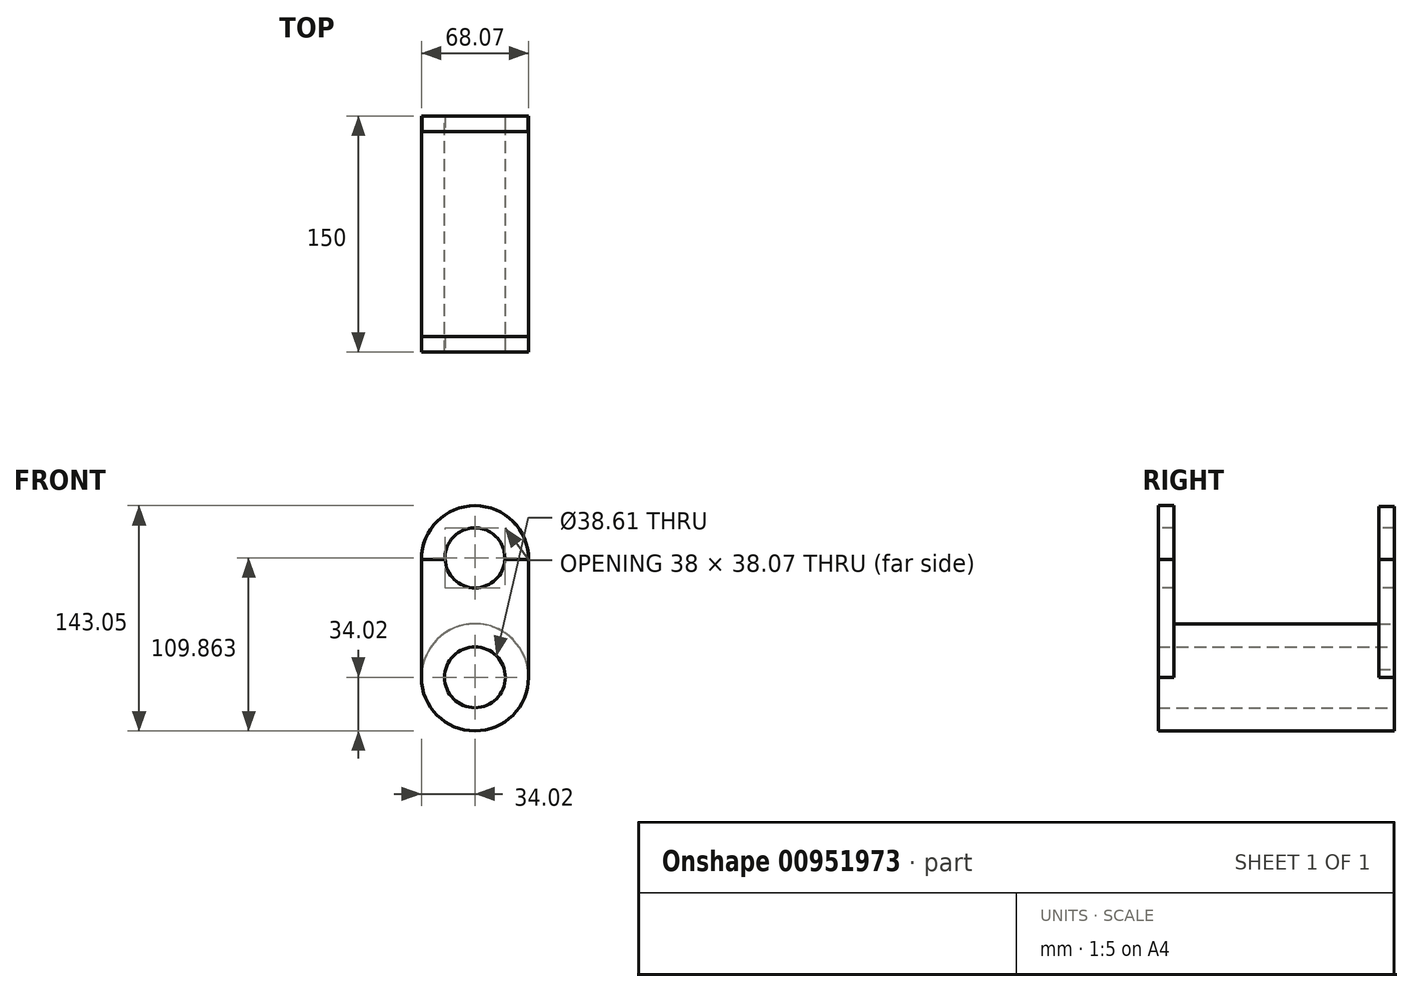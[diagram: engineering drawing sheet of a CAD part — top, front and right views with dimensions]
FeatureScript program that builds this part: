
annotation { "Feature Type Name" : "Feature", "Feature Type Description" : "" }
export const myFeature = defineFeature(function(context is Context, id is Id, definition is map)
    precondition{}
    {
        {
            var Q0;
            Q0=qCreatedBy(makeId("Front.planeOp"),FACE);
            var sketch = newSketch(context, id + "F0", { "sketchPlane" : qUnion([Q0])});
            skCircle(sketch, "E0", {"center": v(0, 0) * mm, "radius": 34.02 * mm});
            skCircle(sketch, "E1", {"center": v(0, 0) * mm, "radius": 19.3 * mm});
            skSolve(sketch);
        }
        {
            var Q0;
            Q0=makeQuery(id+"F0.imprint","IMPRINT",FACE,{"disambiguationData":[TD([[makeQuery(id+"F0.imprint","IMPRINT",EDGE,{"derivedFrom":sQuery(id+"F0.wireOp",EDGE,"E0")}),1.0]])]});
            extrude(context, id + "F1", {"entities" : qUnion([Q0]), "depth" : 75 * mm, "offsetDistance" : 25 * mm});
        }
        {
            var Q0;
            Q0=makeQuery(id+"F1.opExtrude","SWEPT_BODY",BODY,{"disambiguationData":[OSD([sQuery(id+"F0.wireOp",EDGE,"E0"),sQuery(id+"F0.wireOp",EDGE,"E1")])]});
            var Q1;
            Q1=makeQuery(id+"F1.opExtrude","CAP_FACE",FACE,{"disambiguationData":[OSD([sQuery(id+"F0.wireOp",EDGE,"E0"),sQuery(id+"F0.wireOp",EDGE,"E1")])],"isStart":true});
            mirror(context, id + "F2", {"operationType" : NewBodyOperationType.ADD, "entities" : qUnion([Q0]), "mirrorPlane" : qUnion([Q1])});
        }
        {
            var Q0;
            Q0=makeQuery(id+"F1.opExtrude","CAP_FACE",FACE,{"disambiguationData":[OSD([sQuery(id+"F0.wireOp",EDGE,"E0"),sQuery(id+"F0.wireOp",EDGE,"E1")])],"isStart":false});
            var sketch = newSketch(context, id + "F3", { "sketchPlane" : qUnion([Q0])});
            skLineSegment(sketch, "E2.bottom", {"start": v(-34.02, 0) * mm, "end": v(34.05, 0) * mm});
            skLineSegment(sketch, "E2.top", {"start": v(-34.02, 75) * mm, "end": v(34.05, 75) * mm});
            skLineSegment(sketch, "E2.left", {"start": v(-34.02, 0) * mm, "end": v(-34.02, 75) * mm});
            skLineSegment(sketch, "E2.right", {"start": v(34.05, 0) * mm, "end": v(34.05, 75) * mm});
            skSolve(sketch);
        }
        {
            var Q0;
            Q0=makeQuery(id+"F3.imprint","IMPRINT",FACE,{"disambiguationData":[TD([[makeQuery(id+"F3.imprint","IMPRINT",EDGE,{"derivedFrom":sQuery(id+"F3.wireOp",EDGE,"E2.top")}),-1.0]])]});
            extrude(context, id + "F4", {"entities" : qUnion([Q0]), "operationType" : NewBodyOperationType.ADD, "oppositeDirection" : true, "depth" : 10 * mm, "offsetDistance" : 25 * mm});
        }
        {
            var Q0;
            Q0=makeQuery(id+"F2.opPattern","COPY",FACE,{"derivedFrom":makeQuery(id+"F1.opExtrude","CAP_FACE",FACE,{"disambiguationData":[OSD([sQuery(id+"F0.wireOp",EDGE,"E0"),sQuery(id+"F0.wireOp",EDGE,"E1")])],"isStart":false}),"instanceName":"1"});
            var sketch = newSketch(context, id + "F5", { "sketchPlane" : qUnion([Q0])});
            skLineSegment(sketch, "E3.bottom", {"start": v(-34.02, 0) * mm, "end": v(33.65, 0) * mm});
            skLineSegment(sketch, "E3.top", {"start": v(-34.02, 75) * mm, "end": v(33.65, 75) * mm});
            skLineSegment(sketch, "E3.left", {"start": v(-34.02, 0) * mm, "end": v(-34.02, 75) * mm});
            skLineSegment(sketch, "E3.right", {"start": v(33.65, 0) * mm, "end": v(33.65, 75) * mm});
            skSolve(sketch);
        }
        {
            var Q0;
            {var subQ0=sQuery(id+"F5.wireOp",EDGE,"E3.top");Q0=makeQuery(id+"F5.imprint","IMPRINT",FACE,{"disambiguationData":[TD([[makeQuery(id+"F5.imprint","IMPRINT",EDGE,{"derivedFrom":subQ0}),-1.0]])]});}
            extrude(context, id + "F6", {"entities" : qUnion([Q0]), "oppositeDirection" : true, "depth" : 10 * mm, "offsetDistance" : 25 * mm});
        }
        {
            var Q0;
            {var subQ0=sQuery(id+"F0.wireOp",EDGE,"E0");Q0=makeQuery(id+"F4.boolean.opBoolean","MERGE",FACE,{"derivedFrom":[makeQuery(id+"F1.opExtrude","CAP_FACE",FACE,{"disambiguationData":[OSD([subQ0,sQuery(id+"F0.wireOp",EDGE,"E1")])],"isStart":false}),makeQuery(id+"F4.opExtrude","CAP_FACE",FACE,{"disambiguationData":[OSD([subQ0,sQuery(id+"F3.wireOp",EDGE,"E2.bottom"),sQuery(id+"F3.wireOp",EDGE,"E2.top"),sQuery(id+"F3.wireOp",EDGE,"E2.left"),sQuery(id+"F3.wireOp",EDGE,"E2.right")])],"isStart":true})]});}
            var sketch = newSketch(context, id + "F7", { "sketchPlane" : qUnion([Q0])});
            skCircle(sketch, "E4", {"center": v(0.02, 75) * mm, "radius": 34.03 * mm});
            skSolve(sketch);
        }
        {
            var Q0;
            {var subQ1=makeQuery(id+"F4.opExtrude","CAP_EDGE",EDGE,{"disambiguationData":[OSD([sQuery(id+"F3.wireOp",EDGE,"E2.top")])],"isStart":true});Q0=makeQuery(id+"F7.imprint","IMPRINT",FACE,{"disambiguationData":[TD([[makeQuery(id+"F7.imprint","IMPRINT",EDGE,{"derivedFrom":subQ1}),1.0]])]});}
            extrude(context, id + "F8", {"entities" : qUnion([Q0]), "oppositeDirection" : true, "depth" : 10 * mm, "offsetDistance" : 25 * mm});
        }
        {
            var Q0;
            Q0=makeQuery(id+"F6.opExtrude","CAP_FACE",FACE,{"disambiguationData":[OSD([sQuery(id+"F0.wireOp",EDGE,"E0"),sQuery(id+"F5.wireOp",EDGE,"E3.top"),sQuery(id+"F5.wireOp",EDGE,"E3.left"),sQuery(id+"F5.wireOp",EDGE,"E3.right")])],"isStart":true});
            var sketch = newSketch(context, id + "F9", { "sketchPlane" : qUnion([Q0])});
            skCircle(sketch, "E5", {"center": v(0, 75) * mm, "radius": 33.62 * mm});
            skSolve(sketch);
        }
        {
            var Q0;
            {var subQ0=sQuery(id+"F9.wireOp",EDGE,"E5");var subQ1=makeQuery(id+"F6.opExtrude","CAP_EDGE",EDGE,{"disambiguationData":[OSD([sQuery(id+"F5.wireOp",EDGE,"E3.top")])],"isStart":true});var subQ2=makeQuery(id+"F9.imprint","INTERSECT",VERTEX,{"disambiguationData":[OD(0.0)],"derivedFrom":[subQ1,subQ0]});Q0=makeQuery(id+"F9.imprint","IMPRINT",FACE,{"disambiguationData":[TD([[makeQuery(id+"F9.imprint","IMPRINT",EDGE,{"disambiguationData":[TD([[subQ2,1.0]])],"derivedFrom":subQ0}),1.0]])]});}
            extrude(context, id + "F10", {"entities" : qUnion([Q0]), "operationType" : NewBodyOperationType.ADD, "oppositeDirection" : true, "depth" : 10 * mm, "offsetDistance" : 25 * mm});
        }
        {
            var Q0;
            Q0=makeQuery(id+"F8.opExtrude","CAP_FACE",FACE,{"disambiguationData":[OSD([sQuery(id+"F3.wireOp",EDGE,"E2.top"),sQuery(id+"F7.wireOp",EDGE,"E4")])],"isStart":true});
            var sketch = newSketch(context, id + "F11", { "sketchPlane" : qUnion([Q0])});
            skSolve(sketch);
        }
        {
            var Q0;
            Q0=makeQuery(id+"F11.imprint","IMPRINT",FACE,{"disambiguationData":[TD([[makeQuery(id+"F11.imprint","IMPRINT",EDGE,{"derivedFrom":makeQuery(id+"F8.opExtrude","CAP_EDGE",EDGE,{"disambiguationData":[OSD([sQuery(id+"F7.wireOp",EDGE,"E4")])],"isStart":true})}),1.0]])]});
            var sketch = newSketch(context, id + "F12", { "sketchPlane" : qUnion([Q0])});
            skCircle(sketch, "E6", {"center": v(0, 75.8) * mm, "radius": 19 * mm});
            skSolve(sketch);
        }
        {
            var Q0;
            {var subQ0=sQuery(id+"F12.wireOp",EDGE,"E6");var subQ1=makeQuery(id+"F11.imprint","IMPRINT",EDGE,{"derivedFrom":makeQuery(id+"F8.opExtrude","CAP_EDGE",EDGE,{"disambiguationData":[OSD([sQuery(id+"F3.wireOp",EDGE,"E2.top")])],"isStart":true})});var subQ2=makeQuery(id+"F12.imprint","INTERSECT",VERTEX,{"disambiguationData":[OD(0.0)],"derivedFrom":[subQ1,subQ0]});Q0=makeQuery(id+"F12.imprint","IMPRINT",FACE,{"disambiguationData":[TD([[makeQuery(id+"F12.imprint","IMPRINT",EDGE,{"disambiguationData":[TD([[subQ2,1.0]])],"derivedFrom":subQ0}),1.0]])]});}
            var Q1;
            {var subQ0=sQuery(id+"F12.wireOp",EDGE,"E6");var subQ1=makeQuery(id+"F11.imprint","IMPRINT",EDGE,{"derivedFrom":makeQuery(id+"F8.opExtrude","CAP_EDGE",EDGE,{"disambiguationData":[OSD([sQuery(id+"F3.wireOp",EDGE,"E2.top")])],"isStart":true})});var subQ2=makeQuery(id+"F12.imprint","INTERSECT",VERTEX,{"disambiguationData":[OD(0.0)],"derivedFrom":[subQ1,subQ0]});Q1=makeQuery(id+"F12.imprint","IMPRINT",FACE,{"disambiguationData":[TD([[makeQuery(id+"F12.imprint","IMPRINT",EDGE,{"disambiguationData":[TD([[subQ2,-1.0]])],"derivedFrom":subQ0}),1.0]])]});}
            extrude(context, id + "F13", {"entities" : qUnion([Q0, Q1]), "operationType" : NewBodyOperationType.REMOVE, "oppositeDirection" : true, "depth" : 150 * mm, "offsetDistance" : 25 * mm});
        }
        {
            var Q0;
            Q0=makeQuery(id+"F11.imprint","IMPRINT",FACE,{"disambiguationData":[TD([[makeQuery(id+"F11.imprint","IMPRINT",EDGE,{"derivedFrom":makeQuery(id+"F8.opExtrude","CAP_EDGE",EDGE,{"disambiguationData":[OSD([sQuery(id+"F7.wireOp",EDGE,"E4")])],"isStart":true})}),1.0]])]});
            var sketch = newSketch(context, id + "F14", { "sketchPlane" : qUnion([Q0])});
            skCircle(sketch, "E7", {"center": v(0, 75.88) * mm, "radius": 19 * mm});
            skSolve(sketch);
        }
        {
            var Q0;
            {var subQ0=sQuery(id+"F14.wireOp",EDGE,"E7");var subQ1=makeQuery(id+"F11.imprint","IMPRINT",EDGE,{"derivedFrom":makeQuery(id+"F8.opExtrude","CAP_EDGE",EDGE,{"disambiguationData":[OSD([sQuery(id+"F3.wireOp",EDGE,"E2.top")])],"isStart":true})});var subQ2=makeQuery(id+"F14.imprint","INTERSECT",VERTEX,{"disambiguationData":[OD(0.0)],"derivedFrom":[subQ1,subQ0]});Q0=makeQuery(id+"F14.imprint","IMPRINT",FACE,{"disambiguationData":[TD([[makeQuery(id+"F14.imprint","IMPRINT",EDGE,{"disambiguationData":[TD([[subQ2,1.0]])],"derivedFrom":subQ0}),1.0]])]});}
            extrude(context, id + "F15", {"entities" : qUnion([Q0]), "operationType" : NewBodyOperationType.REMOVE, "oppositeDirection" : true, "depth" : 150 * mm, "offsetDistance" : 25 * mm});
        }
    });
